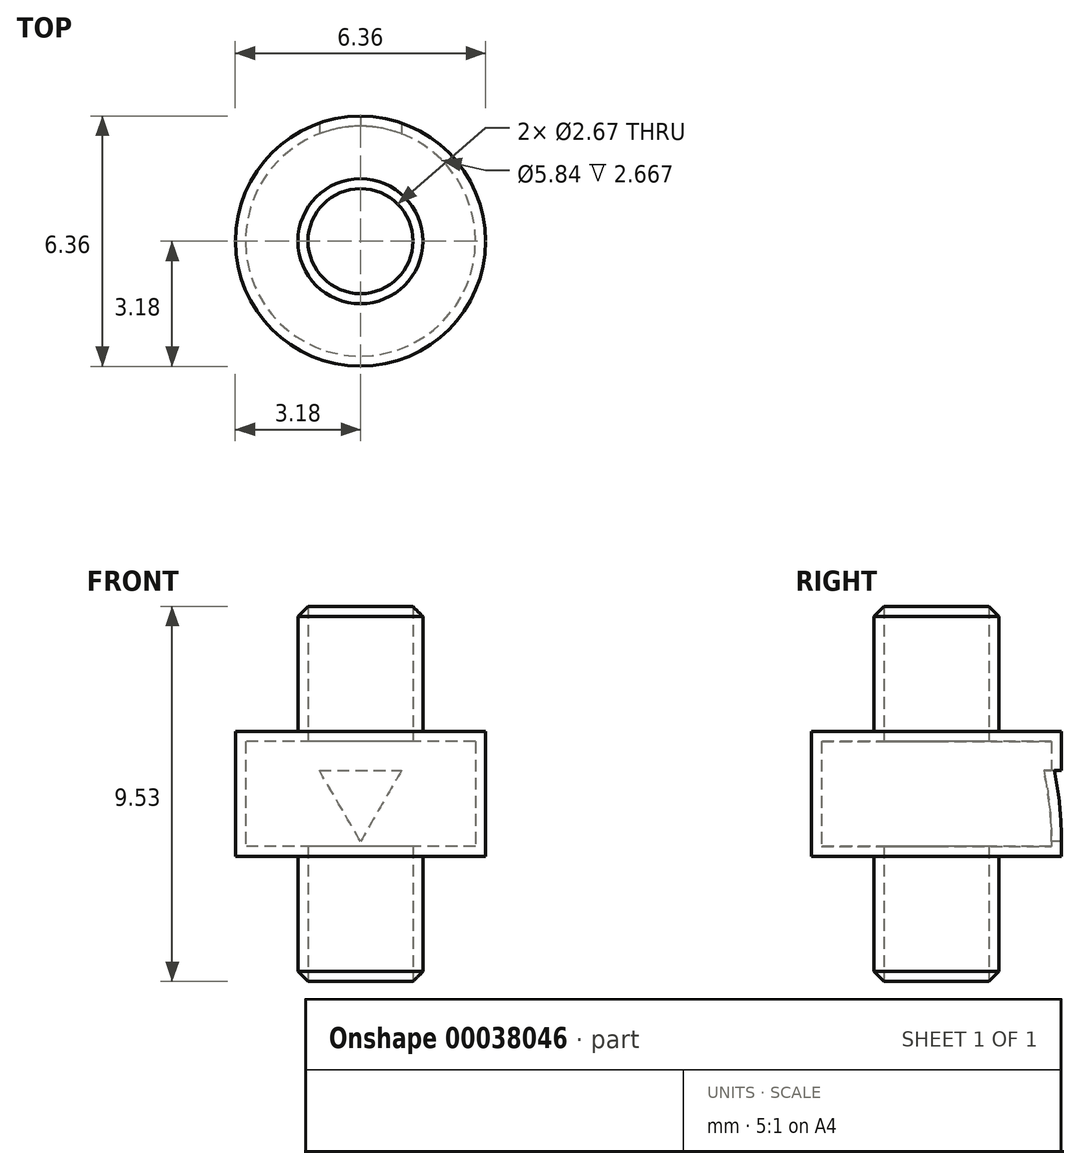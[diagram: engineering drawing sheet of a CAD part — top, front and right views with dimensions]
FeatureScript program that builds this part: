
annotation { "Feature Type Name" : "Feature", "Feature Type Description" : "" }
export const myFeature = defineFeature(function(context is Context, id is Id, definition is map)
    precondition{}
    {
        {
            var Q0;
            Q0=qCreatedBy(makeId("Top.planeOp"),FACE);
            var sketch = newSketch(context, id + "F0", { "sketchPlane" : qUnion([Q0])});
            skCircle(sketch, "E0", {"center": v(0, 0) * mm, "radius": 1.59 * mm});
            skSolve(sketch);
        }
        {
            var Q0;
            Q0 = qSketchRegion(id + "F0", true);
            extrude(context, id + "F1", {"entities" : qUnion([Q0]), "depth" : 3.17 * mm});
        }
        {
            var Q0;
            Q0=makeQuery(id+"F1.opExtrude","CAP_FACE",FACE,{"disambiguationData":[OSD([sQuery(id+"F0.wireOp",EDGE,"E0")])],"isStart":false});
            var sketch = newSketch(context, id + "F2", { "sketchPlane" : qUnion([Q0])});
            skCircle(sketch, "E1", {"center": v(0, 0) * mm, "radius": 3.18 * mm});
            skSolve(sketch);
        }
        {
            var Q0;
            Q0 = qSketchRegion(id + "F2", true);
            extrude(context, id + "F3", {"entities" : qUnion([Q0]), "operationType" : NewBodyOperationType.ADD, "depth" : 3.17 * mm});
        }
        {
            var Q0;
            Q0=makeQuery(id+"F3.opExtrude","CAP_FACE",FACE,{"disambiguationData":[OSD([sQuery(id+"F2.wireOp",EDGE,"E1")])],"isStart":false});
            var sketch = newSketch(context, id + "F4", { "sketchPlane" : qUnion([Q0])});
            skCircle(sketch, "E2", {"center": v(0, 0) * mm, "radius": 1.59 * mm});
            skSolve(sketch);
        }
        {
            var Q0;
            Q0 = qSketchRegion(id + "F4", true);
            extrude(context, id + "F5", {"entities" : qUnion([Q0]), "operationType" : NewBodyOperationType.ADD, "depth" : 3.17 * mm});
        }
        {
            var Q0;
            Q0=makeQuery(id+"F5.opExtrude","CAP_FACE",FACE,{"disambiguationData":[OSD([sQuery(id+"F4.wireOp",EDGE,"E2")])],"isStart":false});
            shell(context, id + "F6", {"entities" : qUnion([Q0]), "thickness" : 0.25 * mm});
        }
        {
            var Q0;
            {var subQ0=sQuery(id+"F0.wireOp",EDGE,"E0");Q0=makeQuery(id+"F6.opShell","OFFSET_FACE",FACE,{"disambiguationData":[OSD([subQ0]),TDD([makeQuery(id+"F1.opExtrude","CAP_FACE",FACE,{"disambiguationData":[OSD([subQ0])],"isStart":true})])]});}
            var Q1;
            Q1=makeQuery(id+"F1.opExtrude","CAP_FACE",FACE,{"disambiguationData":[OSD([sQuery(id+"F0.wireOp",EDGE,"E0")])],"isStart":true});
            extrude(context, id + "F7", {"entities" : qUnion([Q0]), "operationType" : NewBodyOperationType.REMOVE, "endBound" : BoundingType.UP_TO_SURFACE, "oppositeDirection" : true, "endBoundEntityFace" : qUnion([Q1]), "depth" : 25.4 * mm});
        }
        {
            var Q0;
            Q0=makeQuery(id+"F5.opExtrude","CAP_EDGE",EDGE,{"disambiguationData":[OSD([sQuery(id+"F4.wireOp",EDGE,"E2")])],"isStart":false});
            var Q1;
            Q1=makeQuery(id+"F1.opExtrude","CAP_EDGE",EDGE,{"disambiguationData":[OSD([sQuery(id+"F0.wireOp",EDGE,"E0")])],"isStart":true});
            chamfer(context, id + "F8", {"entities" : qUnion([Q0, Q1]), "width" : 0.25 * mm, "tangentPropagation" : true});
        }
        {
            var Q0;
            Q0=qCreatedBy(makeId("Front.planeOp"),FACE);
            var sketch = newSketch(context, id + "F9", { "sketchPlane" : qUnion([Q0])});
            skLineSegment(sketch, "E3", {"start": v(0, 3.18) * mm, "end": v(0, 6.35) * mm, "construction": true});
            skCircle(sketch, "E4.cCircle", {"center": v(0, 4.76) * mm, "radius": 0.6 * mm, "construction": true});
            skLineSegment(sketch, "E4.0", {"start": v(-1.04, 5.37) * mm, "end": v(1.04, 5.37) * mm});
            skLineSegment(sketch, "E4.1", {"start": v(1.04, 5.37) * mm, "end": v(0, 3.56) * mm});
            skLineSegment(sketch, "E4.2", {"start": v(0, 3.56) * mm, "end": v(-1.04, 5.37) * mm});
            skPoint(sketch, "E4.0.midPoint", {"position": v(0, 5.37) * mm});
            skSolve(sketch);
        }
        {
            var Q0;
            Q0 = qSketchRegion(id + "F9", true);
            var Q1;
            Q1=makeQuery(id+"F3.opExtrude","SWEPT_FACE",FACE,{"disambiguationData":[OSD([sQuery(id+"F2.wireOp",EDGE,"E1")])]});
            extrude(context, id + "F10", {"entities" : qUnion([Q0]), "operationType" : NewBodyOperationType.REMOVE, "endBound" : BoundingType.UP_TO_SURFACE, "oppositeDirection" : true, "endBoundEntityFace" : qUnion([Q1]), "depth" : 25.4 * mm});
        }
    });
